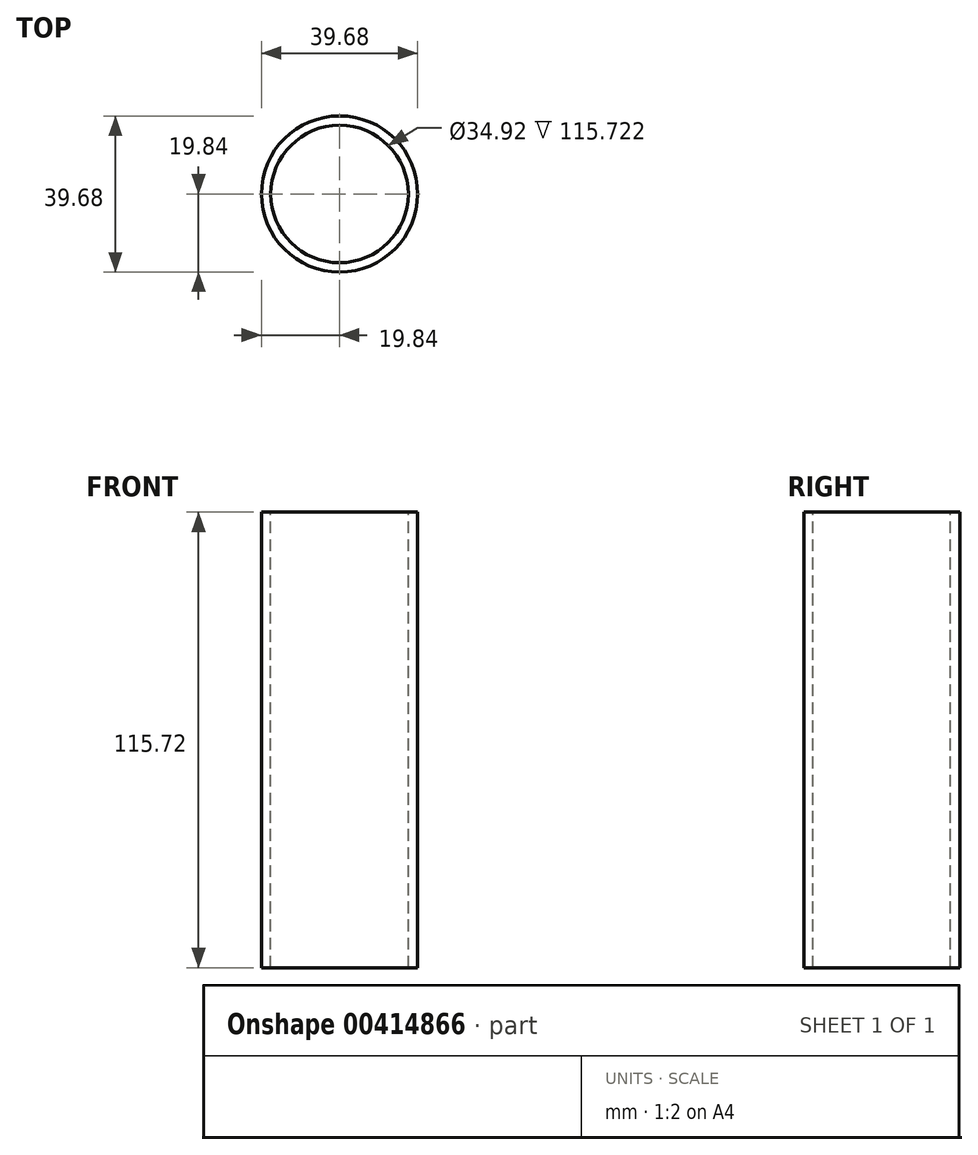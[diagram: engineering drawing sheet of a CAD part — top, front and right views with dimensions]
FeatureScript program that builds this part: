
annotation { "Feature Type Name" : "Feature", "Feature Type Description" : "" }
export const myFeature = defineFeature(function(context is Context, id is Id, definition is map)
    precondition{}
    {
        {
            var Q0;
            Q0=qCreatedBy(makeId("Top.planeOp"),FACE);
            var sketch = newSketch(context, id + "F0", { "sketchPlane" : qUnion([Q0])});
            skCircle(sketch, "E0", {"center": v(0, 0) * mm, "radius": 19.84 * mm});
            skCircle(sketch, "E1", {"center": v(0, 0) * mm, "radius": 17.46 * mm});
            skSolve(sketch);
        }
        {
            var Q0;
            Q0 = qSketchRegion(id + "F0", true);
            extrude(context, id + "F1", {"entities" : qUnion([Q0]), "oppositeDirection" : true, "depth" : 115.72 * mm});
        }
    });
